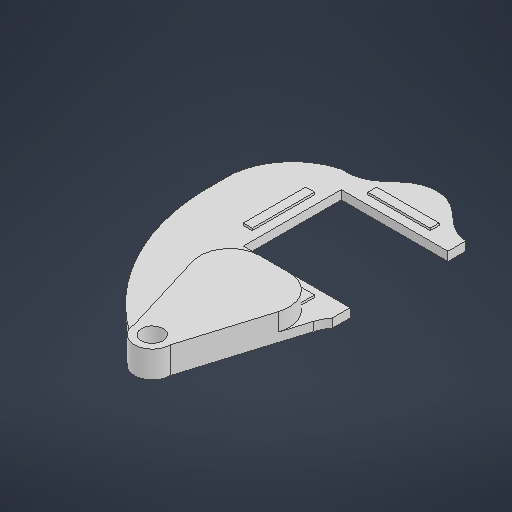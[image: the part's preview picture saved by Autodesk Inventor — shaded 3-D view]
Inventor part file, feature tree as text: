
AUTODESK INVENTOR PART (.ipt)
format: ipt  version: 2025.1 (Build 291241000, 241)  size: 721,408 bytes
history: native  units: in
note: dims shown in document units (in); Inventor stores cm internally (conversion verified against a paired STEP export)
features: projected_geometry x35, extrude x5, sketch x3, fillet x3
ambient origin geometry x8: Origin, YZ Plane, XZ Plane, XY Plane, X Axis, Y Axis, Z Axis, Center Point
bodies: Solid1 (feature_tree)
feature tree (46):
  sketch  "Sketch1"  dims[d0=0.1909in d1=0.315in]
  extrude  "Extrusion1"  Depth=0.315in
  extrude  "Extrusion2"  Depth=1.6732in
  extrude  "Extrusion3"  Depth=0.0787in
  extrude  "Extrusion4"  Depth=0.0787in
  fillet  "Fillet1"  Radius=1.1811in
  extrude  "Extrusion5"  Depth=0.0787in
  fillet  "Fillet2"  Radius=0.5512in
  fillet  "Fillet3"  Radius=0.2362in
  sketch  "Sketch2"  dims[d2=2.622in d3=1.6732in]
  sketch  "Sketch3"  dims[d4=1.0236in d5=1.0236in d6=1.1811in d7=1.1811in d8=0.5512in d9=0.5512in d10=0.2362in d11=0.0in d12=0.0787in d13=0.0in d14=0.0984in d15=0.0in d16=0.8661in d17=0.0787in d18=0.0984in d19=0.0in d20=0.2662in d21=0.1575in d22=0.0787in d23=0.0in d24=0.3287in d25=0.0787in]
  projected_geometry  "Projected Loop1"
  projected_geometry  "Projected Loop2"
  projected_geometry  "Projected Loop3"
  projected_geometry  "Projected Loop4"
  projected_geometry  "Projected Loop5"
  projected_geometry  "Projected Loop6"
  projected_geometry  "Projected Loop7"
  projected_geometry  "Projected Loop8"
  projected_geometry  "Projected Loop9"
  projected_geometry  "Projected Loop10"
  projected_geometry  "Projected Loop11"
  projected_geometry  "Projected Loop12"
  projected_geometry  "Projected Loop13"
  projected_geometry  "Projected Loop14"
  projected_geometry  "Projected Loop15"
  projected_geometry  "Projected Loop16"
  projected_geometry  "Projected Loop17"
  projected_geometry  "Projected Loop18"
  projected_geometry  "Projected Loop19"
  projected_geometry  "Projected Loop20"
  projected_geometry  "Projected Loop21"
  projected_geometry  "Projected Loop22"
  projected_geometry  "Projected Loop23"
  projected_geometry  "Projected Loop24"
  projected_geometry  "Projected Loop25"
  projected_geometry  "Projected Loop26"
  projected_geometry  "Projected Loop27"
  projected_geometry  "Projected Loop28"
  projected_geometry  "Projected Loop29"
  projected_geometry  "Projected Loop30"
  projected_geometry  "Projected Loop31"
  projected_geometry  "Projected Loop32"
  projected_geometry  "Projected Loop33"
  projected_geometry  "Projected Loop34"
  projected_geometry  "Projected Loop35"
